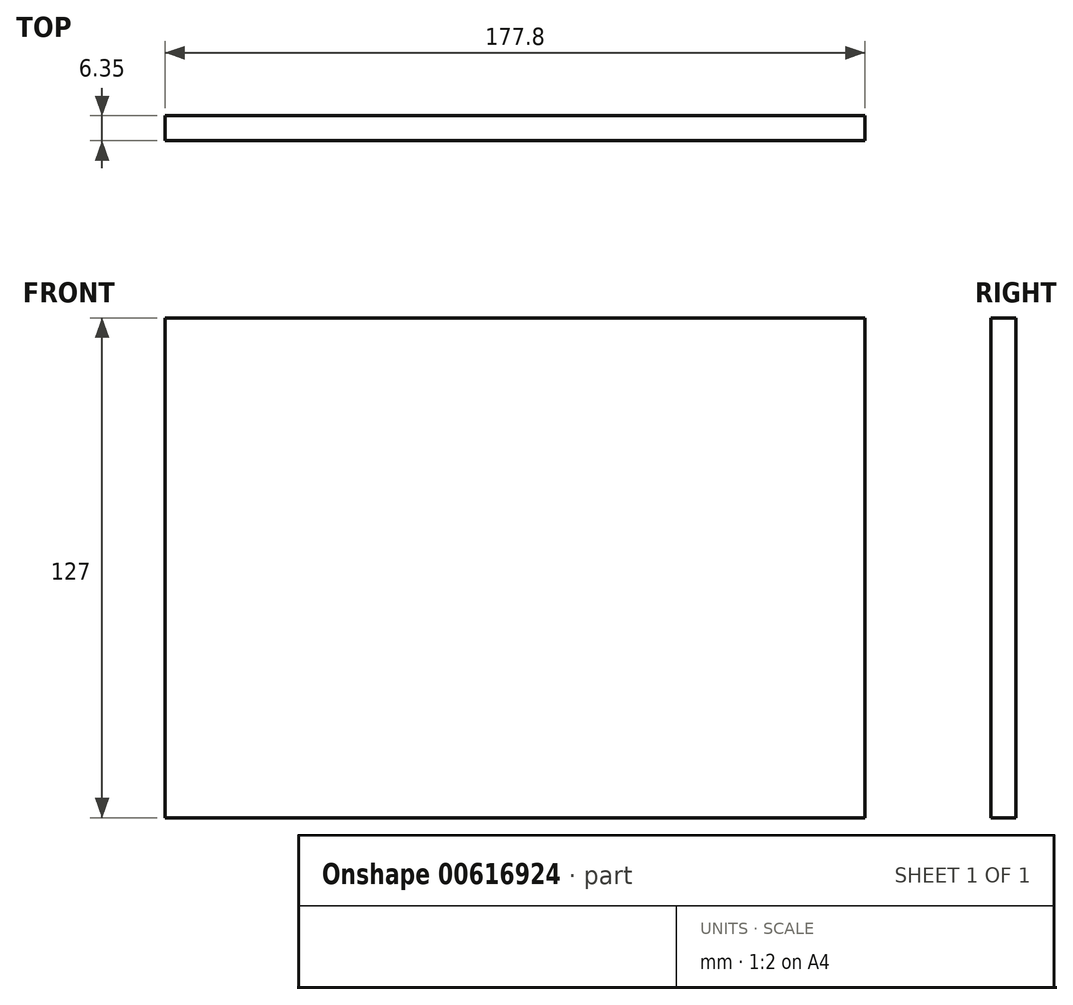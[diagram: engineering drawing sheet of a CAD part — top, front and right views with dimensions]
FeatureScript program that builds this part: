
annotation { "Feature Type Name" : "Feature", "Feature Type Description" : "" }
export const myFeature = defineFeature(function(context is Context, id is Id, definition is map)
    precondition{}
    {
        {
            var Q0;
            Q0=qCreatedBy(makeId("Front.planeOp"),FACE);
            var sketch = newSketch(context, id + "F0", { "sketchPlane" : qUnion([Q0])});
            skLineSegment(sketch, "E0", {"start": v(-88.9, 0) * mm, "end": v(88.9, 0) * mm});
            skLineSegment(sketch, "E1", {"start": v(88.9, 0) * mm, "end": v(88.9, 127) * mm});
            skLineSegment(sketch, "E2", {"start": v(88.9, 127) * mm, "end": v(-88.9, 127) * mm});
            skLineSegment(sketch, "E3", {"start": v(-88.9, 127) * mm, "end": v(-88.9, 0) * mm});
            skSolve(sketch);
        }
        {
            var Q0;
            Q0=makeQuery(id+"F0.imprint","IMPRINT",FACE,{"disambiguationData":[TD([[makeQuery(id+"F0.imprint","IMPRINT",EDGE,{"derivedFrom":sQuery(id+"F0.wireOp",EDGE,"E0")}),1.0]])]});
            extrude(context, id + "F1", {"entities" : qUnion([Q0]), "depth" : 6.35 * mm, "offsetDistance" : 25.4 * mm});
        }
    });
